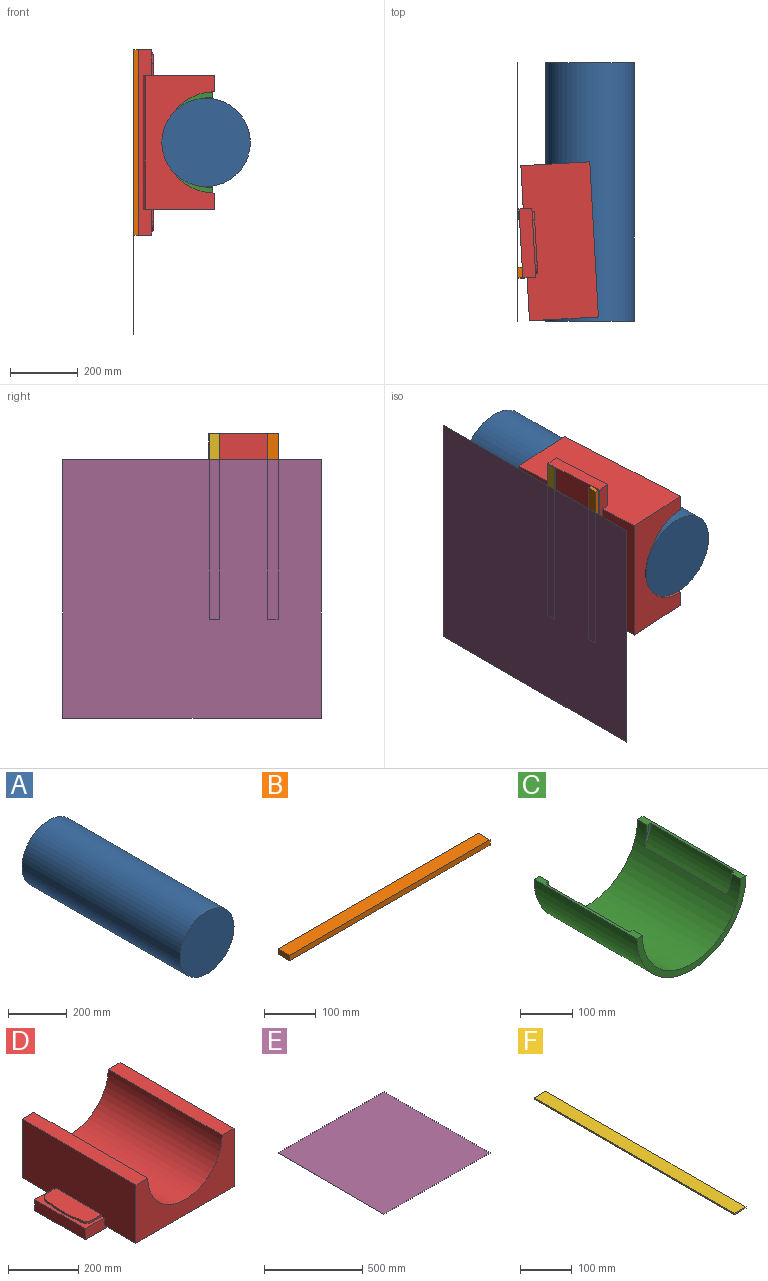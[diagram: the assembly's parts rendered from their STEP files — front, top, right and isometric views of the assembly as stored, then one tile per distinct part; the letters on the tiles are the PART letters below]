
ASSEMBLY  parts=6 mates=6
PART A: 3 faces, bbox 260.4x762x260.4 mm
  f0: cylinder r=130.18mm len=762mm, axis (0,1,0), area 623250.2mm2, adj f1,f2
  f1: plane 260.35x260.35mm, normal (0,-1,0), area 53236mm2, adj f0
  f2: plane 260.35x260.35mm, normal (0,1,0), area 53236mm2, adj f0
PART B: 6 faces, bbox 546.1x31.8x12.7 mm
  f0: plane 546.1x12.7mm, normal (0,1,0), area 6935.5mm2, adj f1,f3,f4,f5
  f1: plane 31.75x12.7mm, normal (-1,0,0), area 403.2mm2, adj f0,f2,f4,f5
  f2: plane 546.1x12.7mm, normal (0,-1,0), area 6935.5mm2, adj f1,f3,f4,f5
  f3: plane 31.75x12.7mm, normal (1,0,0), area 403.2mm2, adj f0,f2,f4,f5
  f4: plane 546.1x31.75mm, normal (0,0,1), area 17338.7mm2, adj f0,f1,f2,f3
  f5: plane 546.1x31.75mm, normal (0,0,-1), area 17338.7mm2, adj f0,f1,f2,f3
PART C: 16 faces, bbox 296.6x279.8x148.6 mm
  f0: plane 279.81x14.76mm, normal (0,0,1), area 2099.1mm2, adj f1,f2,f4,f5,f9,f10,f11,f14
  f1: cylinder r=133.53mm len=279.81mm, axis (0,-1,0), area 95204.3mm2, adj f0,f3,f4,f5,f6,f7,f8,f9
  f2: cylinder r=148.28mm len=296.57mm, axis (0,-1,0), area 130346.9mm2, adj f0,f3,f4,f5
  f3: plane 279.81x14.76mm, normal (0,0,1), area 2099.1mm2, adj f1,f2,f4,f5,f6,f7,f8,f12
  f4: plane 296.57x148.28mm, normal (0,1,0), area 6532mm2, adj f0,f1,f2,f3
  f5: plane 296.57x148.28mm, normal (0,-1,0), area 6532mm2, adj f0,f1,f2,f3
  f6: cylinder r=96.16mm len=222.66mm, axis (0,-1,0), area 11422.6mm2, adj f1,f3,f12,f13
  f7: plane 34.84x10.35mm, normal (0,-1,0), area 115.9mm2, adj f1,f3,f13
  f8: plane 34.84x10.35mm, normal (0,1,0), area 115.9mm2, adj f1,f3,f12
  f9: cylinder r=96.16mm len=222.66mm, axis (0,-1,0), area 11422.6mm2, adj f0,f1,f14,f15
  f10: plane 34.84x10.35mm, normal (0,-1,0), area 115.9mm2, adj f0,f1,f15
  f11: plane 34.84x10.35mm, normal (0,1,0), area 115.9mm2, adj f0,f1,f14
  f12: cone r=96.16mm half-angle=45deg, axis (0,1,0), area 197.9mm2, adj f1,f3,f6,f8
  f13: cone r=92.99mm half-angle=45deg, axis (0,-1,0), area 197.9mm2, adj f1,f3,f6,f7
  f14: cone r=92.99mm half-angle=45deg, axis (0,1,0), area 197.9mm2, adj f0,f1,f9,f11
  f15: cone r=96.16mm half-angle=45deg, axis (0,-1,0), area 197.9mm2, adj f0,f1,f9,f10
PART D: 28 faces, bbox 546.1x457.6x215.9 mm
  f0: plane 546.1x203.2mm, normal (0,0,-1), area 110967.5mm2, adj f6,f7,f8,f9
  f1: plane 457.61x47.63mm, normal (0,0,1), area 21793.5mm2, adj f2,f3,f22,f25
  f2: plane 393.7x203.2mm, normal (0,-1,0), area 45021.2mm2, adj f1,f22,f23,f24,f25,f27
  f3: plane 393.7x203.2mm, normal (0,1,0), area 45021.2mm2, adj f1,f22,f23,f24,f25,f26
  f4: plane 203.2x76.2mm, normal (0,0,1), area 3859.8mm2, adj f7,f8,f9,f16,f17,f18,f19,f20
  f5: plane 203.2x76.2mm, normal (0,0,1), area 3859.8mm2, adj f6,f8,f9,f10,f11,f12,f13,f14
  f6: plane 203.2x38.1mm, normal (-1,0,0), area 7741.9mm2, adj f0,f5,f8,f9
  f7: plane 203.2x38.1mm, normal (1,0,0), area 7741.9mm2, adj f0,f4,f8,f9
  f8: plane 546.1x38.1mm, normal (0,1,0), area 10806.4mm2, adj f0,f4,f5,f6,f7,f22,f23,f26
  f9: plane 546.1x38.1mm, normal (0,-1,0), area 10806.4mm2, adj f0,f4,f5,f6,f7,f22,f23,f27
  f10: cylinder r=25.4mm len=25.4mm, axis (0,0,-1), area 253.4mm2, adj f5,f11,f14,f15
  f11: cylinder r=457.2mm len=133.35mm, axis (0,0,-1), area 849.8mm2, adj f5,f10,f12,f15
  f12: cylinder r=25.4mm len=25.4mm, axis (0,0,-1), area 253.4mm2, adj f5,f11,f13,f15
  f13: plane 36.86x6.35mm, normal (0,-1,0), area 234.1mm2, adj f5,f12,f15,f22
  f14: plane 36.86x6.35mm, normal (0,1,0), area 234.1mm2, adj f5,f10,f15,f22
  f15: plane 184.15x67.15mm, normal (0,0,1), area 11624mm2, adj f10,f11,f12,f13,f14,f22
  f16: cylinder r=25.4mm len=25.4mm, axis (0,0,-1), area 253.4mm2, adj f4,f17,f20,f21
  f17: cylinder r=457.2mm len=133.35mm, axis (0,0,-1), area 849.8mm2, adj f4,f16,f18,f21
  f18: cylinder r=25.4mm len=25.4mm, axis (0,0,-1), area 253.4mm2, adj f4,f17,f19,f21
  f19: plane 36.86x6.35mm, normal (0,1,0), area 234.1mm2, adj f4,f18,f21,f23
  f20: plane 36.86x6.35mm, normal (0,-1,0), area 234.1mm2, adj f4,f16,f21,f23
  f21: plane 184.15x67.15mm, normal (0,0,1), area 11624mm2, adj f16,f17,f18,f19,f20,f23
  f22: plane 457.61x203.2mm, normal (-1,0,0), area 86655mm2, adj f1,f2,f3,f5,f8,f9,f13,f14
  f23: plane 457.61x203.2mm, normal (1,0,0), area 86655mm2, adj f2,f3,f4,f8,f9,f19,f20,f21
  f24: plane 457.61x47.63mm, normal (0,0,1), area 21793.5mm2, adj f2,f3,f23,f25
  f25: cylinder r=149.22mm len=457.61mm, axis (0,1,0), area 214527.8mm2, adj f1,f2,f3,f24
  f26: plane 393.7x127.2mm, normal (0,0,-1), area 50079.9mm2, adj f3,f8,f22,f23
  f27: plane 393.7x127.2mm, normal (0,0,-1), area 50079.9mm2, adj f2,f9,f22,f23
PART E: 6 faces, bbox 762x762x0.3 mm
  f0: plane 762x0.25mm, normal (0,1,0), area 193.5mm2, adj f1,f3,f4,f5
  f1: plane 762x0.25mm, normal (-1,0,0), area 193.5mm2, adj f0,f2,f4,f5
  f2: plane 762x0.25mm, normal (0,-1,0), area 193.5mm2, adj f1,f3,f4,f5
  f3: plane 762x0.25mm, normal (1,0,0), area 193.5mm2, adj f0,f2,f4,f5
  f4: plane 762x762mm, normal (0,0,1), area 580644mm2, adj f0,f1,f2,f3
  f5: plane 762x762mm, normal (0,0,-1), area 580644mm2, adj f0,f1,f2,f3
PART F: 6 faces, bbox 31.8x546.1x3.2 mm
  f0: plane 546.1x3.18mm, normal (1,0,0), area 1733.9mm2, adj f1,f3,f4,f5
  f1: plane 31.75x3.18mm, normal (0,1,0), area 100.8mm2, adj f0,f2,f4,f5
  f2: plane 546.1x3.18mm, normal (-1,0,0), area 1733.9mm2, adj f1,f3,f4,f5
  f3: plane 31.75x3.18mm, normal (0,-1,0), area 100.8mm2, adj f0,f2,f4,f5
  f4: plane 546.1x31.75mm, normal (0,0,1), area 17338.7mm2, adj f0,f1,f2,f3
  f5: plane 546.1x31.75mm, normal (0,0,-1), area 17338.7mm2, adj f0,f1,f2,f3
PLACE A rot(axis=(0,0,-1),0deg) t=(142.06,1410.92,552.32)mm
PLACE B rot(axis=(0.71,0,0.71),180deg) t=(-70.54,792.05,552.4)mm
PLACE C rot(axis=(-0.03,1,0.03),90deg) t=(161.62,749.92,552.4)mm
PLACE D rot(axis=(-0.03,1,0.03),90deg) t=(-56.08,776.17,552.4)mm
PLACE E rot(axis=(0,1,0),90deg) t=(-70.8,961.97,372.15)mm fixed
PLACE F rot(axis=(-0.58,-0.58,0.58),120deg) t=(-68.95,963.81,552.4)mm
MATE fastened E.f4 <-> F.f4  axis (1,0,0) through (-70.55,648.92,749.17)mm
MATE parallel F.f5 <-> B.f4  axis (1,0,0) through (-67.37,947.62,825.45)mm
MATE fastened C.f1 <-> D.f25  axis (0.06,-1,0) through (161.62,749.92,552.4)mm
MATE parallel E.f4 <-> B.f5  axis (1,0,0) through (-70.55,648.92,749.17)mm
MATE fastened A.f0 <-> E.f2  axis (0,-1,0) through (142.05,648.92,552.32)mm
MATE fastened B.f5 <-> E.f4  axis (1,0,0) through (-70.54,776.17,825.45)mm
